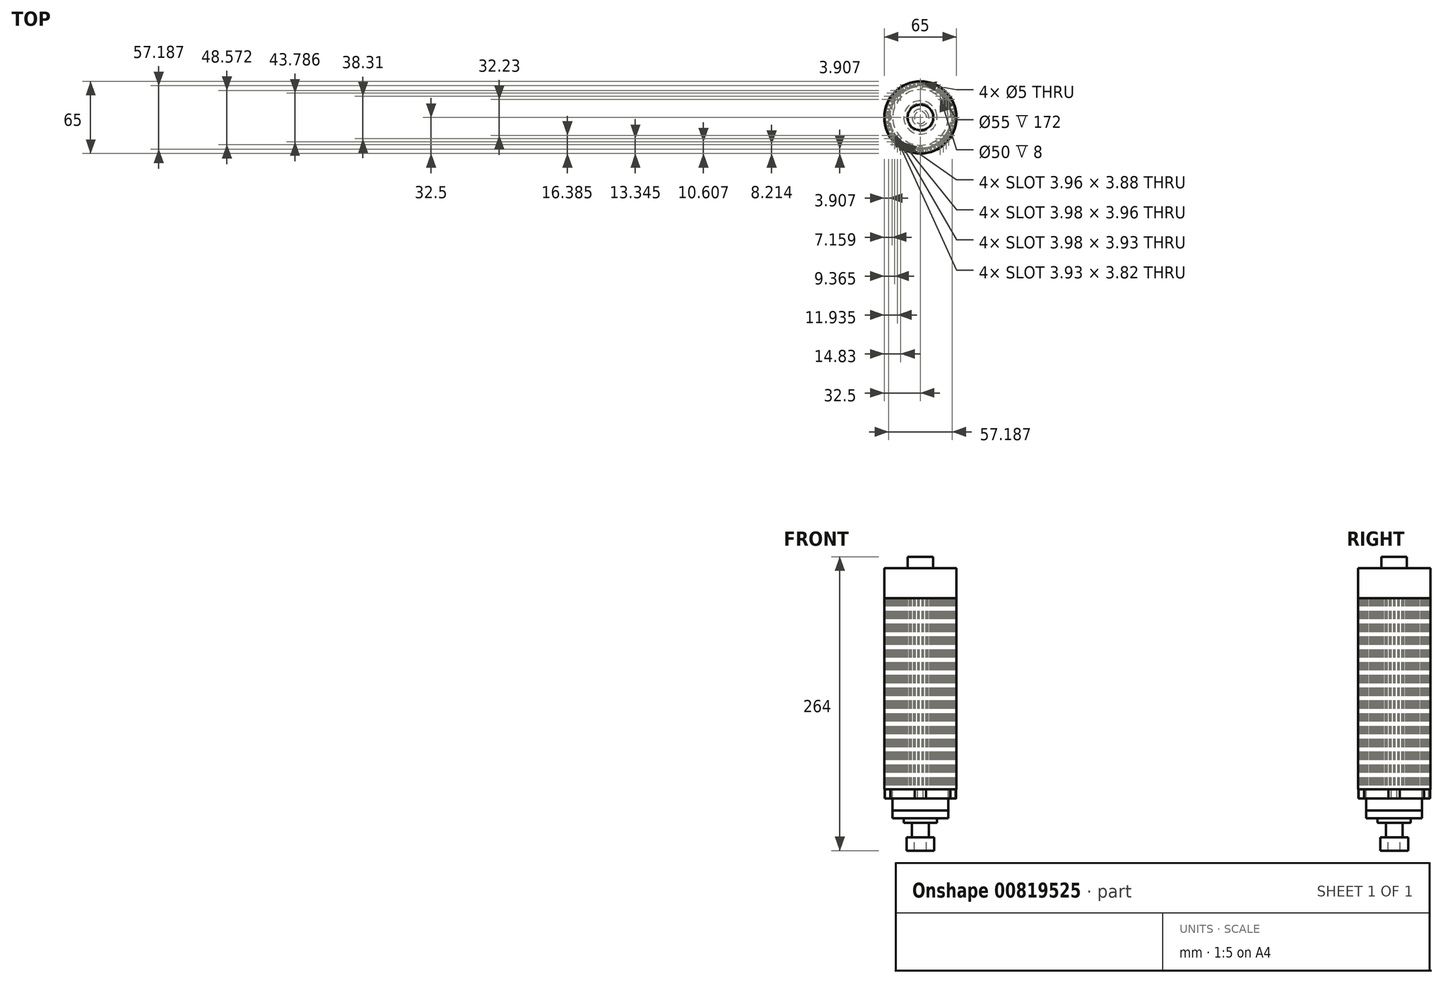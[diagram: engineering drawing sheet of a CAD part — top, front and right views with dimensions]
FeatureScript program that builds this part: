
annotation { "Feature Type Name" : "Feature", "Feature Type Description" : "" }
export const myFeature = defineFeature(function(context is Context, id is Id, definition is map)
    precondition{}
    {
        {
            var Q0;
            Q0=qCreatedBy(makeId("Top.planeOp"),FACE);
            var sketch = newSketch(context, id + "F0", { "sketchPlane" : qUnion([Q0])});
            skCircle(sketch, "E0", {"center": v(0, 0) * mm, "radius": 27.5 * mm});
            skCircle(sketch, "E1", {"center": v(0, 0) * mm, "radius": 32.5 * mm});
            skArc(sketch, "E2", {"start": v(1.37, 31.47) * mm, "mid": v(0, 31.5) * mm, "end": v(-1.37, 31.47) * mm});
            skArc(sketch, "E3", {"start": v(1.24, 28.47) * mm, "mid": v(0, 28.5) * mm, "end": v(-1.24, 28.47) * mm});
            skLineSegment(sketch, "E4", {"start": v(-1.37, 31.47) * mm, "end": v(-1.24, 28.47) * mm});
            skLineSegment(sketch, "E5", {"start": v(-1.24, 28.47) * mm, "end": v(0, 0) * mm, "construction": true});
            skLineSegment(sketch, "E6", {"start": v(0, 0) * mm, "end": v(1.24, 28.47) * mm, "construction": true});
            skLineSegment(sketch, "E7", {"start": v(1.24, 28.47) * mm, "end": v(1.37, 31.47) * mm});
            skArc(sketch, "E8.1.0", {"start": v(-2.58, 31.4) * mm, "mid": v(-3.95, 31.25) * mm, "end": v(-5.3, 31.05) * mm});
            skLineSegment(sketch, "E8.1.1", {"start": v(-5.3, 31.05) * mm, "end": v(-4.8, 28.1) * mm});
            skArc(sketch, "E8.1.2", {"start": v(-2.34, 28.4) * mm, "mid": v(-3.57, 28.28) * mm, "end": v(-4.8, 28.1) * mm});
            skLineSegment(sketch, "E8.1.3", {"start": v(-2.34, 28.4) * mm, "end": v(-2.58, 31.4) * mm});
            skArc(sketch, "E8.2.0", {"start": v(-6.5, 30.82) * mm, "mid": v(-7.83, 30.51) * mm, "end": v(-9.16, 30.14) * mm});
            skLineSegment(sketch, "E8.2.1", {"start": v(-9.16, 30.14) * mm, "end": v(-8.29, 27.27) * mm});
            skArc(sketch, "E8.2.2", {"start": v(-5.88, 27.89) * mm, "mid": v(-7.09, 27.6) * mm, "end": v(-8.29, 27.27) * mm});
            skLineSegment(sketch, "E8.2.3", {"start": v(-5.88, 27.89) * mm, "end": v(-6.5, 30.82) * mm});
            skArc(sketch, "E8.3.0", {"start": v(-10.3, 29.77) * mm, "mid": v(-11.6, 29.29) * mm, "end": v(-12.86, 28.75) * mm});
            skLineSegment(sketch, "E8.3.1", {"start": v(-12.86, 28.75) * mm, "end": v(-11.64, 26.02) * mm});
            skArc(sketch, "E8.3.2", {"start": v(-9.33, 26.93) * mm, "mid": v(-10.5, 26.5) * mm, "end": v(-11.64, 26.02) * mm});
            skLineSegment(sketch, "E8.3.3", {"start": v(-9.33, 26.93) * mm, "end": v(-10.3, 29.77) * mm});
            skArc(sketch, "E8.4.0", {"start": v(-13.96, 28.24) * mm, "mid": v(-15.18, 27.6) * mm, "end": v(-16.36, 26.92) * mm});
            skLineSegment(sketch, "E8.4.1", {"start": v(-16.36, 26.92) * mm, "end": v(-14.8, 24.35) * mm});
            skArc(sketch, "E8.4.2", {"start": v(-12.63, 25.55) * mm, "mid": v(-13.73, 24.97) * mm, "end": v(-14.8, 24.35) * mm});
            skLineSegment(sketch, "E8.4.3", {"start": v(-12.63, 25.55) * mm, "end": v(-13.96, 28.24) * mm});
            skArc(sketch, "E8.5.0", {"start": v(-17.39, 26.27) * mm, "mid": v(-18.52, 25.48) * mm, "end": v(-19.6, 24.65) * mm});
            skLineSegment(sketch, "E8.5.1", {"start": v(-19.6, 24.65) * mm, "end": v(-17.74, 22.3) * mm});
            skArc(sketch, "E8.5.2", {"start": v(-15.73, 23.77) * mm, "mid": v(-16.75, 23.06) * mm, "end": v(-17.74, 22.3) * mm});
            skLineSegment(sketch, "E8.5.3", {"start": v(-15.73, 23.77) * mm, "end": v(-17.39, 26.27) * mm});
            skArc(sketch, "E8.6.0", {"start": v(-20.54, 23.88) * mm, "mid": v(-21.56, 22.96) * mm, "end": v(-22.54, 22) * mm});
            skLineSegment(sketch, "E8.6.1", {"start": v(-22.54, 22) * mm, "end": v(-20.4, 19.9) * mm});
            skArc(sketch, "E8.6.2", {"start": v(-18.58, 21.6) * mm, "mid": v(-19.5, 20.78) * mm, "end": v(-20.4, 19.9) * mm});
            skLineSegment(sketch, "E8.6.3", {"start": v(-18.58, 21.6) * mm, "end": v(-20.54, 23.88) * mm});
            skArc(sketch, "E8.7.0", {"start": v(-23.37, 21.12) * mm, "mid": v(-24.27, 20.08) * mm, "end": v(-25.12, 19) * mm});
            skLineSegment(sketch, "E8.7.1", {"start": v(-25.12, 19) * mm, "end": v(-22.73, 17.2) * mm});
            skArc(sketch, "E8.7.2", {"start": v(-21.15, 19.1) * mm, "mid": v(-21.96, 18.17) * mm, "end": v(-22.73, 17.2) * mm});
            skLineSegment(sketch, "E8.7.3", {"start": v(-21.15, 19.1) * mm, "end": v(-23.37, 21.12) * mm});
            skArc(sketch, "E8.8.0", {"start": v(-25.83, 18.02) * mm, "mid": v(-26.6, 16.88) * mm, "end": v(-27.3, 15.7) * mm});
            skLineSegment(sketch, "E8.8.1", {"start": v(-27.3, 15.7) * mm, "end": v(-24.7, 14.2) * mm});
            skArc(sketch, "E8.8.2", {"start": v(-23.37, 16.3) * mm, "mid": v(-24.06, 15.27) * mm, "end": v(-24.7, 14.2) * mm});
            skLineSegment(sketch, "E8.8.3", {"start": v(-23.37, 16.3) * mm, "end": v(-25.83, 18.02) * mm});
            skArc(sketch, "E8.9.0", {"start": v(-27.89, 14.64) * mm, "mid": v(-28.5, 13.41) * mm, "end": v(-29.06, 12.16) * mm});
            skLineSegment(sketch, "E8.9.1", {"start": v(-29.06, 12.16) * mm, "end": v(-26.3, 11) * mm});
            skArc(sketch, "E8.9.2", {"start": v(-25.23, 13.25) * mm, "mid": v(-25.79, 12.13) * mm, "end": v(-26.3, 11) * mm});
            skLineSegment(sketch, "E8.9.3", {"start": v(-25.23, 13.25) * mm, "end": v(-27.89, 14.64) * mm});
            skArc(sketch, "E8.10.0", {"start": v(-29.5, 11.03) * mm, "mid": v(-29.96, 9.73) * mm, "end": v(-30.35, 8.42) * mm});
            skLineSegment(sketch, "E8.10.1", {"start": v(-30.35, 8.42) * mm, "end": v(-27.46, 7.62) * mm});
            skArc(sketch, "E8.10.2", {"start": v(-26.7, 9.98) * mm, "mid": v(-27.1, 8.8) * mm, "end": v(-27.46, 7.62) * mm});
            skLineSegment(sketch, "E8.10.3", {"start": v(-26.7, 9.98) * mm, "end": v(-29.5, 11.03) * mm});
            skArc(sketch, "E8.11.0", {"start": v(-30.66, 7.25) * mm, "mid": v(-30.94, 5.9) * mm, "end": v(-31.17, 4.55) * mm});
            skLineSegment(sketch, "E8.11.1", {"start": v(-31.17, 4.55) * mm, "end": v(-28.2, 4.11) * mm});
            skArc(sketch, "E8.11.2", {"start": v(-27.74, 6.56) * mm, "mid": v(-28, 5.34) * mm, "end": v(-28.2, 4.11) * mm});
            skLineSegment(sketch, "E8.11.3", {"start": v(-27.74, 6.56) * mm, "end": v(-30.66, 7.25) * mm});
            skArc(sketch, "E8.12.0", {"start": v(-31.32, 3.35) * mm, "mid": v(-31.44, 1.98) * mm, "end": v(-31.5, 0.6) * mm});
            skLineSegment(sketch, "E8.12.1", {"start": v(-31.5, 0.6) * mm, "end": v(-28.5, 0.55) * mm});
            skArc(sketch, "E8.12.2", {"start": v(-28.34, 3.03) * mm, "mid": v(-28.44, 1.79) * mm, "end": v(-28.5, 0.55) * mm});
            skLineSegment(sketch, "E8.12.3", {"start": v(-28.34, 3.03) * mm, "end": v(-31.32, 3.35) * mm});
            skArc(sketch, "E8.13.0", {"start": v(-31.5, -0.6) * mm, "mid": v(-31.44, -1.98) * mm, "end": v(-31.32, -3.35) * mm});
            skLineSegment(sketch, "E8.13.1", {"start": v(-31.32, -3.35) * mm, "end": v(-28.34, -3.03) * mm});
            skArc(sketch, "E8.13.2", {"start": v(-28.5, -0.55) * mm, "mid": v(-28.44, -1.79) * mm, "end": v(-28.34, -3.03) * mm});
            skLineSegment(sketch, "E8.13.3", {"start": v(-28.5, -0.55) * mm, "end": v(-31.5, -0.6) * mm});
            skArc(sketch, "E8.14.0", {"start": v(-31.17, -4.55) * mm, "mid": v(-30.94, -5.9) * mm, "end": v(-30.66, -7.25) * mm});
            skLineSegment(sketch, "E8.14.1", {"start": v(-30.66, -7.25) * mm, "end": v(-27.74, -6.56) * mm});
            skArc(sketch, "E8.14.2", {"start": v(-28.2, -4.11) * mm, "mid": v(-28, -5.34) * mm, "end": v(-27.74, -6.56) * mm});
            skLineSegment(sketch, "E8.14.3", {"start": v(-28.2, -4.11) * mm, "end": v(-31.17, -4.55) * mm});
            skArc(sketch, "E8.15.0", {"start": v(-30.35, -8.42) * mm, "mid": v(-29.96, -9.73) * mm, "end": v(-29.5, -11.03) * mm});
            skLineSegment(sketch, "E8.15.1", {"start": v(-29.5, -11.03) * mm, "end": v(-26.7, -9.98) * mm});
            skArc(sketch, "E8.15.2", {"start": v(-27.46, -7.62) * mm, "mid": v(-27.1, -8.8) * mm, "end": v(-26.7, -9.98) * mm});
            skLineSegment(sketch, "E8.15.3", {"start": v(-27.46, -7.62) * mm, "end": v(-30.35, -8.42) * mm});
            skArc(sketch, "E8.16.0", {"start": v(-29.06, -12.16) * mm, "mid": v(-28.5, -13.41) * mm, "end": v(-27.89, -14.64) * mm});
            skLineSegment(sketch, "E8.16.1", {"start": v(-27.89, -14.64) * mm, "end": v(-25.23, -13.25) * mm});
            skArc(sketch, "E8.16.2", {"start": v(-26.3, -11) * mm, "mid": v(-25.79, -12.13) * mm, "end": v(-25.23, -13.25) * mm});
            skLineSegment(sketch, "E8.16.3", {"start": v(-26.3, -11) * mm, "end": v(-29.06, -12.16) * mm});
            skArc(sketch, "E8.17.0", {"start": v(-27.3, -15.7) * mm, "mid": v(-26.6, -16.88) * mm, "end": v(-25.83, -18.02) * mm});
            skLineSegment(sketch, "E8.17.1", {"start": v(-25.83, -18.02) * mm, "end": v(-23.37, -16.3) * mm});
            skArc(sketch, "E8.17.2", {"start": v(-24.7, -14.2) * mm, "mid": v(-24.06, -15.27) * mm, "end": v(-23.37, -16.3) * mm});
            skLineSegment(sketch, "E8.17.3", {"start": v(-24.7, -14.2) * mm, "end": v(-27.3, -15.7) * mm});
            skArc(sketch, "E8.18.0", {"start": v(-25.12, -19) * mm, "mid": v(-24.27, -20.08) * mm, "end": v(-23.37, -21.12) * mm});
            skLineSegment(sketch, "E8.18.1", {"start": v(-23.37, -21.12) * mm, "end": v(-21.15, -19.1) * mm});
            skArc(sketch, "E8.18.2", {"start": v(-22.73, -17.2) * mm, "mid": v(-21.96, -18.17) * mm, "end": v(-21.15, -19.1) * mm});
            skLineSegment(sketch, "E8.18.3", {"start": v(-22.73, -17.2) * mm, "end": v(-25.12, -19) * mm});
            skArc(sketch, "E8.19.0", {"start": v(-22.54, -22) * mm, "mid": v(-21.56, -22.96) * mm, "end": v(-20.54, -23.88) * mm});
            skLineSegment(sketch, "E8.19.1", {"start": v(-20.54, -23.88) * mm, "end": v(-18.58, -21.6) * mm});
            skArc(sketch, "E8.19.2", {"start": v(-20.4, -19.9) * mm, "mid": v(-19.5, -20.78) * mm, "end": v(-18.58, -21.6) * mm});
            skLineSegment(sketch, "E8.19.3", {"start": v(-20.4, -19.9) * mm, "end": v(-22.54, -22) * mm});
            skArc(sketch, "E8.20.0", {"start": v(-19.6, -24.65) * mm, "mid": v(-18.52, -25.48) * mm, "end": v(-17.39, -26.27) * mm});
            skLineSegment(sketch, "E8.20.1", {"start": v(-17.39, -26.27) * mm, "end": v(-15.73, -23.77) * mm});
            skArc(sketch, "E8.20.2", {"start": v(-17.74, -22.3) * mm, "mid": v(-16.75, -23.06) * mm, "end": v(-15.73, -23.77) * mm});
            skLineSegment(sketch, "E8.20.3", {"start": v(-17.74, -22.3) * mm, "end": v(-19.6, -24.65) * mm});
            skArc(sketch, "E8.21.0", {"start": v(-16.36, -26.92) * mm, "mid": v(-15.18, -27.6) * mm, "end": v(-13.96, -28.24) * mm});
            skLineSegment(sketch, "E8.21.1", {"start": v(-13.96, -28.24) * mm, "end": v(-12.63, -25.55) * mm});
            skArc(sketch, "E8.21.2", {"start": v(-14.8, -24.35) * mm, "mid": v(-13.73, -24.97) * mm, "end": v(-12.63, -25.55) * mm});
            skLineSegment(sketch, "E8.21.3", {"start": v(-14.8, -24.35) * mm, "end": v(-16.36, -26.92) * mm});
            skArc(sketch, "E8.22.0", {"start": v(-12.86, -28.75) * mm, "mid": v(-11.6, -29.29) * mm, "end": v(-10.3, -29.77) * mm});
            skLineSegment(sketch, "E8.22.1", {"start": v(-10.3, -29.77) * mm, "end": v(-9.33, -26.93) * mm});
            skArc(sketch, "E8.22.2", {"start": v(-11.64, -26.02) * mm, "mid": v(-10.5, -26.5) * mm, "end": v(-9.33, -26.93) * mm});
            skLineSegment(sketch, "E8.22.3", {"start": v(-11.64, -26.02) * mm, "end": v(-12.86, -28.75) * mm});
            skArc(sketch, "E8.23.0", {"start": v(-9.16, -30.14) * mm, "mid": v(-7.83, -30.51) * mm, "end": v(-6.5, -30.82) * mm});
            skLineSegment(sketch, "E8.23.1", {"start": v(-6.5, -30.82) * mm, "end": v(-5.88, -27.89) * mm});
            skArc(sketch, "E8.23.2", {"start": v(-8.29, -27.27) * mm, "mid": v(-7.09, -27.6) * mm, "end": v(-5.88, -27.89) * mm});
            skLineSegment(sketch, "E8.23.3", {"start": v(-8.29, -27.27) * mm, "end": v(-9.16, -30.14) * mm});
            skArc(sketch, "E8.24.0", {"start": v(-5.3, -31.05) * mm, "mid": v(-3.95, -31.25) * mm, "end": v(-2.58, -31.4) * mm});
            skLineSegment(sketch, "E8.24.1", {"start": v(-2.58, -31.4) * mm, "end": v(-2.34, -28.4) * mm});
            skArc(sketch, "E8.24.2", {"start": v(-4.8, -28.1) * mm, "mid": v(-3.57, -28.28) * mm, "end": v(-2.34, -28.4) * mm});
            skLineSegment(sketch, "E8.24.3", {"start": v(-4.8, -28.1) * mm, "end": v(-5.3, -31.05) * mm});
            skArc(sketch, "E8.25.0", {"start": v(-1.37, -31.47) * mm, "mid": v(0, -31.5) * mm, "end": v(1.37, -31.47) * mm});
            skLineSegment(sketch, "E8.25.1", {"start": v(1.37, -31.47) * mm, "end": v(1.24, -28.47) * mm});
            skArc(sketch, "E8.25.2", {"start": v(-1.24, -28.47) * mm, "mid": v(0, -28.5) * mm, "end": v(1.24, -28.47) * mm});
            skLineSegment(sketch, "E8.25.3", {"start": v(-1.24, -28.47) * mm, "end": v(-1.37, -31.47) * mm});
            skArc(sketch, "E8.26.0", {"start": v(2.58, -31.4) * mm, "mid": v(3.95, -31.25) * mm, "end": v(5.3, -31.05) * mm});
            skLineSegment(sketch, "E8.26.1", {"start": v(5.3, -31.05) * mm, "end": v(4.8, -28.1) * mm});
            skArc(sketch, "E8.26.2", {"start": v(2.34, -28.4) * mm, "mid": v(3.57, -28.28) * mm, "end": v(4.8, -28.1) * mm});
            skLineSegment(sketch, "E8.26.3", {"start": v(2.34, -28.4) * mm, "end": v(2.58, -31.4) * mm});
            skArc(sketch, "E8.27.0", {"start": v(6.5, -30.82) * mm, "mid": v(7.83, -30.51) * mm, "end": v(9.16, -30.14) * mm});
            skLineSegment(sketch, "E8.27.1", {"start": v(9.16, -30.14) * mm, "end": v(8.29, -27.27) * mm});
            skArc(sketch, "E8.27.2", {"start": v(5.88, -27.89) * mm, "mid": v(7.09, -27.6) * mm, "end": v(8.29, -27.27) * mm});
            skLineSegment(sketch, "E8.27.3", {"start": v(5.88, -27.89) * mm, "end": v(6.5, -30.82) * mm});
            skArc(sketch, "E8.28.0", {"start": v(10.3, -29.77) * mm, "mid": v(11.6, -29.29) * mm, "end": v(12.86, -28.75) * mm});
            skLineSegment(sketch, "E8.28.1", {"start": v(12.86, -28.75) * mm, "end": v(11.64, -26.02) * mm});
            skArc(sketch, "E8.28.2", {"start": v(9.33, -26.93) * mm, "mid": v(10.5, -26.5) * mm, "end": v(11.64, -26.02) * mm});
            skLineSegment(sketch, "E8.28.3", {"start": v(9.33, -26.93) * mm, "end": v(10.3, -29.77) * mm});
            skArc(sketch, "E8.29.0", {"start": v(13.96, -28.24) * mm, "mid": v(15.18, -27.6) * mm, "end": v(16.36, -26.92) * mm});
            skLineSegment(sketch, "E8.29.1", {"start": v(16.36, -26.92) * mm, "end": v(14.8, -24.35) * mm});
            skArc(sketch, "E8.29.2", {"start": v(12.63, -25.55) * mm, "mid": v(13.73, -24.97) * mm, "end": v(14.8, -24.35) * mm});
            skLineSegment(sketch, "E8.29.3", {"start": v(12.63, -25.55) * mm, "end": v(13.96, -28.24) * mm});
            skArc(sketch, "E8.30.0", {"start": v(17.39, -26.27) * mm, "mid": v(18.52, -25.48) * mm, "end": v(19.6, -24.65) * mm});
            skLineSegment(sketch, "E8.30.1", {"start": v(19.6, -24.65) * mm, "end": v(17.74, -22.3) * mm});
            skArc(sketch, "E8.30.2", {"start": v(15.73, -23.77) * mm, "mid": v(16.75, -23.06) * mm, "end": v(17.74, -22.3) * mm});
            skLineSegment(sketch, "E8.30.3", {"start": v(15.73, -23.77) * mm, "end": v(17.39, -26.27) * mm});
            skArc(sketch, "E8.31.0", {"start": v(20.54, -23.88) * mm, "mid": v(21.56, -22.96) * mm, "end": v(22.54, -22) * mm});
            skLineSegment(sketch, "E8.31.1", {"start": v(22.54, -22) * mm, "end": v(20.4, -19.9) * mm});
            skArc(sketch, "E8.31.2", {"start": v(18.58, -21.6) * mm, "mid": v(19.5, -20.78) * mm, "end": v(20.4, -19.9) * mm});
            skLineSegment(sketch, "E8.31.3", {"start": v(18.58, -21.6) * mm, "end": v(20.54, -23.88) * mm});
            skArc(sketch, "E8.32.0", {"start": v(23.37, -21.12) * mm, "mid": v(24.27, -20.08) * mm, "end": v(25.12, -19) * mm});
            skLineSegment(sketch, "E8.32.1", {"start": v(25.12, -19) * mm, "end": v(22.73, -17.2) * mm});
            skArc(sketch, "E8.32.2", {"start": v(21.15, -19.1) * mm, "mid": v(21.96, -18.17) * mm, "end": v(22.73, -17.2) * mm});
            skLineSegment(sketch, "E8.32.3", {"start": v(21.15, -19.1) * mm, "end": v(23.37, -21.12) * mm});
            skArc(sketch, "E8.33.0", {"start": v(25.83, -18.02) * mm, "mid": v(26.6, -16.88) * mm, "end": v(27.3, -15.7) * mm});
            skLineSegment(sketch, "E8.33.1", {"start": v(27.3, -15.7) * mm, "end": v(24.7, -14.2) * mm});
            skArc(sketch, "E8.33.2", {"start": v(23.37, -16.3) * mm, "mid": v(24.06, -15.27) * mm, "end": v(24.7, -14.2) * mm});
            skLineSegment(sketch, "E8.33.3", {"start": v(23.37, -16.3) * mm, "end": v(25.83, -18.02) * mm});
            skArc(sketch, "E8.34.0", {"start": v(27.89, -14.64) * mm, "mid": v(28.5, -13.41) * mm, "end": v(29.06, -12.16) * mm});
            skLineSegment(sketch, "E8.34.1", {"start": v(29.06, -12.16) * mm, "end": v(26.3, -11) * mm});
            skArc(sketch, "E8.34.2", {"start": v(25.23, -13.25) * mm, "mid": v(25.79, -12.13) * mm, "end": v(26.3, -11) * mm});
            skLineSegment(sketch, "E8.34.3", {"start": v(25.23, -13.25) * mm, "end": v(27.89, -14.64) * mm});
            skArc(sketch, "E8.35.0", {"start": v(29.5, -11.03) * mm, "mid": v(29.96, -9.73) * mm, "end": v(30.35, -8.42) * mm});
            skLineSegment(sketch, "E8.35.1", {"start": v(30.35, -8.42) * mm, "end": v(27.46, -7.62) * mm});
            skArc(sketch, "E8.35.2", {"start": v(26.7, -9.98) * mm, "mid": v(27.1, -8.8) * mm, "end": v(27.46, -7.62) * mm});
            skLineSegment(sketch, "E8.35.3", {"start": v(26.7, -9.98) * mm, "end": v(29.5, -11.03) * mm});
            skArc(sketch, "E8.36.0", {"start": v(30.66, -7.25) * mm, "mid": v(30.94, -5.9) * mm, "end": v(31.17, -4.55) * mm});
            skLineSegment(sketch, "E8.36.1", {"start": v(31.17, -4.55) * mm, "end": v(28.2, -4.11) * mm});
            skArc(sketch, "E8.36.2", {"start": v(27.74, -6.56) * mm, "mid": v(28, -5.34) * mm, "end": v(28.2, -4.11) * mm});
            skLineSegment(sketch, "E8.36.3", {"start": v(27.74, -6.56) * mm, "end": v(30.66, -7.25) * mm});
            skArc(sketch, "E8.37.0", {"start": v(31.32, -3.35) * mm, "mid": v(31.44, -1.98) * mm, "end": v(31.5, -0.6) * mm});
            skLineSegment(sketch, "E8.37.1", {"start": v(31.5, -0.6) * mm, "end": v(28.5, -0.55) * mm});
            skArc(sketch, "E8.37.2", {"start": v(28.34, -3.03) * mm, "mid": v(28.44, -1.79) * mm, "end": v(28.5, -0.55) * mm});
            skLineSegment(sketch, "E8.37.3", {"start": v(28.34, -3.03) * mm, "end": v(31.32, -3.35) * mm});
            skArc(sketch, "E8.38.0", {"start": v(31.5, 0.6) * mm, "mid": v(31.44, 1.98) * mm, "end": v(31.32, 3.35) * mm});
            skLineSegment(sketch, "E8.38.1", {"start": v(31.32, 3.35) * mm, "end": v(28.34, 3.03) * mm});
            skArc(sketch, "E8.38.2", {"start": v(28.5, 0.55) * mm, "mid": v(28.44, 1.79) * mm, "end": v(28.34, 3.03) * mm});
            skLineSegment(sketch, "E8.38.3", {"start": v(28.5, 0.55) * mm, "end": v(31.5, 0.6) * mm});
            skArc(sketch, "E8.39.0", {"start": v(31.17, 4.55) * mm, "mid": v(30.94, 5.9) * mm, "end": v(30.66, 7.25) * mm});
            skLineSegment(sketch, "E8.39.1", {"start": v(30.66, 7.25) * mm, "end": v(27.74, 6.56) * mm});
            skArc(sketch, "E8.39.2", {"start": v(28.2, 4.11) * mm, "mid": v(28, 5.34) * mm, "end": v(27.74, 6.56) * mm});
            skLineSegment(sketch, "E8.39.3", {"start": v(28.2, 4.11) * mm, "end": v(31.17, 4.55) * mm});
            skArc(sketch, "E8.40.0", {"start": v(30.35, 8.42) * mm, "mid": v(29.96, 9.73) * mm, "end": v(29.5, 11.03) * mm});
            skLineSegment(sketch, "E8.40.1", {"start": v(29.5, 11.03) * mm, "end": v(26.7, 9.98) * mm});
            skArc(sketch, "E8.40.2", {"start": v(27.46, 7.62) * mm, "mid": v(27.1, 8.8) * mm, "end": v(26.7, 9.98) * mm});
            skLineSegment(sketch, "E8.40.3", {"start": v(27.46, 7.62) * mm, "end": v(30.35, 8.42) * mm});
            skArc(sketch, "E8.41.0", {"start": v(29.06, 12.16) * mm, "mid": v(28.5, 13.41) * mm, "end": v(27.89, 14.64) * mm});
            skLineSegment(sketch, "E8.41.1", {"start": v(27.89, 14.64) * mm, "end": v(25.23, 13.25) * mm});
            skArc(sketch, "E8.41.2", {"start": v(26.3, 11) * mm, "mid": v(25.79, 12.13) * mm, "end": v(25.23, 13.25) * mm});
            skLineSegment(sketch, "E8.41.3", {"start": v(26.3, 11) * mm, "end": v(29.06, 12.16) * mm});
            skArc(sketch, "E8.42.0", {"start": v(27.3, 15.7) * mm, "mid": v(26.6, 16.88) * mm, "end": v(25.83, 18.02) * mm});
            skLineSegment(sketch, "E8.42.1", {"start": v(25.83, 18.02) * mm, "end": v(23.37, 16.3) * mm});
            skArc(sketch, "E8.42.2", {"start": v(24.7, 14.2) * mm, "mid": v(24.06, 15.27) * mm, "end": v(23.37, 16.3) * mm});
            skLineSegment(sketch, "E8.42.3", {"start": v(24.7, 14.2) * mm, "end": v(27.3, 15.7) * mm});
            skArc(sketch, "E8.43.0", {"start": v(25.12, 19) * mm, "mid": v(24.27, 20.08) * mm, "end": v(23.37, 21.12) * mm});
            skLineSegment(sketch, "E8.43.1", {"start": v(23.37, 21.12) * mm, "end": v(21.15, 19.1) * mm});
            skArc(sketch, "E8.43.2", {"start": v(22.73, 17.2) * mm, "mid": v(21.96, 18.17) * mm, "end": v(21.15, 19.1) * mm});
            skLineSegment(sketch, "E8.43.3", {"start": v(22.73, 17.2) * mm, "end": v(25.12, 19) * mm});
            skArc(sketch, "E8.44.0", {"start": v(22.54, 22) * mm, "mid": v(21.56, 22.96) * mm, "end": v(20.54, 23.88) * mm});
            skLineSegment(sketch, "E8.44.1", {"start": v(20.54, 23.88) * mm, "end": v(18.58, 21.6) * mm});
            skArc(sketch, "E8.44.2", {"start": v(20.4, 19.9) * mm, "mid": v(19.5, 20.78) * mm, "end": v(18.58, 21.6) * mm});
            skLineSegment(sketch, "E8.44.3", {"start": v(20.4, 19.9) * mm, "end": v(22.54, 22) * mm});
            skArc(sketch, "E8.45.0", {"start": v(19.6, 24.65) * mm, "mid": v(18.52, 25.48) * mm, "end": v(17.39, 26.27) * mm});
            skLineSegment(sketch, "E8.45.1", {"start": v(17.39, 26.27) * mm, "end": v(15.73, 23.77) * mm});
            skArc(sketch, "E8.45.2", {"start": v(17.74, 22.3) * mm, "mid": v(16.75, 23.06) * mm, "end": v(15.73, 23.77) * mm});
            skLineSegment(sketch, "E8.45.3", {"start": v(17.74, 22.3) * mm, "end": v(19.6, 24.65) * mm});
            skArc(sketch, "E8.46.0", {"start": v(16.36, 26.92) * mm, "mid": v(15.18, 27.6) * mm, "end": v(13.96, 28.24) * mm});
            skLineSegment(sketch, "E8.46.1", {"start": v(13.96, 28.24) * mm, "end": v(12.63, 25.55) * mm});
            skArc(sketch, "E8.46.2", {"start": v(14.8, 24.35) * mm, "mid": v(13.73, 24.97) * mm, "end": v(12.63, 25.55) * mm});
            skLineSegment(sketch, "E8.46.3", {"start": v(14.8, 24.35) * mm, "end": v(16.36, 26.92) * mm});
            skArc(sketch, "E8.47.0", {"start": v(12.86, 28.75) * mm, "mid": v(11.6, 29.29) * mm, "end": v(10.3, 29.77) * mm});
            skLineSegment(sketch, "E8.47.1", {"start": v(10.3, 29.77) * mm, "end": v(9.33, 26.93) * mm});
            skArc(sketch, "E8.47.2", {"start": v(11.64, 26.02) * mm, "mid": v(10.5, 26.5) * mm, "end": v(9.33, 26.93) * mm});
            skLineSegment(sketch, "E8.47.3", {"start": v(11.64, 26.02) * mm, "end": v(12.86, 28.75) * mm});
            skArc(sketch, "E8.48.0", {"start": v(9.16, 30.14) * mm, "mid": v(7.83, 30.51) * mm, "end": v(6.5, 30.82) * mm});
            skLineSegment(sketch, "E8.48.1", {"start": v(6.5, 30.82) * mm, "end": v(5.88, 27.89) * mm});
            skArc(sketch, "E8.48.2", {"start": v(8.29, 27.27) * mm, "mid": v(7.09, 27.6) * mm, "end": v(5.88, 27.89) * mm});
            skLineSegment(sketch, "E8.48.3", {"start": v(8.29, 27.27) * mm, "end": v(9.16, 30.14) * mm});
            skArc(sketch, "E8.49.0", {"start": v(5.3, 31.05) * mm, "mid": v(3.95, 31.25) * mm, "end": v(2.58, 31.4) * mm});
            skLineSegment(sketch, "E8.49.1", {"start": v(2.58, 31.4) * mm, "end": v(2.34, 28.4) * mm});
            skArc(sketch, "E8.49.2", {"start": v(4.8, 28.1) * mm, "mid": v(3.57, 28.28) * mm, "end": v(2.34, 28.4) * mm});
            skLineSegment(sketch, "E8.49.3", {"start": v(4.8, 28.1) * mm, "end": v(5.3, 31.05) * mm});
            skSolve(sketch);
        }
        {
            var Q0;
            Q0=makeQuery(id+"F0.imprint","IMPRINT",FACE,{"disambiguationData":[TD([[makeQuery(id+"F0.imprint","IMPRINT",EDGE,{"derivedFrom":sQuery(id+"F0.wireOp",EDGE,"E0")}),-1.0]])]});
            extrude(context, id + "F1", {"entities" : qUnion([Q0]), "depth" : 172 * mm, "offsetDistance" : 25.4 * mm});
        }
        {
            var Q0;
            Q0=makeQuery(id+"F1.opExtrude","CAP_FACE",FACE,{"disambiguationData":[OSD([sQuery(id+"F0.wireOp",EDGE,"E0"),sQuery(id+"F0.wireOp",EDGE,"E1"),sQuery(id+"F0.wireOp",EDGE,"E2"),sQuery(id+"F0.wireOp",EDGE,"E3"),sQuery(id+"F0.wireOp",EDGE,"E4"),sQuery(id+"F0.wireOp",EDGE,"E7"),sQuery(id+"F0.wireOp",EDGE,"E8.1.0"),sQuery(id+"F0.wireOp",EDGE,"E8.1.1"),sQuery(id+"F0.wireOp",EDGE,"E8.1.2"),sQuery(id+"F0.wireOp",EDGE,"E8.1.3"),sQuery(id+"F0.wireOp",EDGE,"E8.2.0"),sQuery(id+"F0.wireOp",EDGE,"E8.2.1"),sQuery(id+"F0.wireOp",EDGE,"E8.2.2"),sQuery(id+"F0.wireOp",EDGE,"E8.2.3"),sQuery(id+"F0.wireOp",EDGE,"E8.3.0"),sQuery(id+"F0.wireOp",EDGE,"E8.3.1"),sQuery(id+"F0.wireOp",EDGE,"E8.3.2"),sQuery(id+"F0.wireOp",EDGE,"E8.3.3"),sQuery(id+"F0.wireOp",EDGE,"E8.4.0"),sQuery(id+"F0.wireOp",EDGE,"E8.4.1"),sQuery(id+"F0.wireOp",EDGE,"E8.4.2"),sQuery(id+"F0.wireOp",EDGE,"E8.4.3"),sQuery(id+"F0.wireOp",EDGE,"E8.5.0"),sQuery(id+"F0.wireOp",EDGE,"E8.5.1"),sQuery(id+"F0.wireOp",EDGE,"E8.5.2"),sQuery(id+"F0.wireOp",EDGE,"E8.5.3"),sQuery(id+"F0.wireOp",EDGE,"E8.6.0"),sQuery(id+"F0.wireOp",EDGE,"E8.6.1"),sQuery(id+"F0.wireOp",EDGE,"E8.6.2"),sQuery(id+"F0.wireOp",EDGE,"E8.6.3"),sQuery(id+"F0.wireOp",EDGE,"E8.7.0"),sQuery(id+"F0.wireOp",EDGE,"E8.7.1"),sQuery(id+"F0.wireOp",EDGE,"E8.7.2"),sQuery(id+"F0.wireOp",EDGE,"E8.7.3"),sQuery(id+"F0.wireOp",EDGE,"E8.8.0"),sQuery(id+"F0.wireOp",EDGE,"E8.8.1"),sQuery(id+"F0.wireOp",EDGE,"E8.8.2"),sQuery(id+"F0.wireOp",EDGE,"E8.8.3"),sQuery(id+"F0.wireOp",EDGE,"E8.9.0"),sQuery(id+"F0.wireOp",EDGE,"E8.9.1"),sQuery(id+"F0.wireOp",EDGE,"E8.9.2"),sQuery(id+"F0.wireOp",EDGE,"E8.9.3"),sQuery(id+"F0.wireOp",EDGE,"E8.10.0"),sQuery(id+"F0.wireOp",EDGE,"E8.10.1"),sQuery(id+"F0.wireOp",EDGE,"E8.10.2"),sQuery(id+"F0.wireOp",EDGE,"E8.10.3"),sQuery(id+"F0.wireOp",EDGE,"E8.11.0"),sQuery(id+"F0.wireOp",EDGE,"E8.11.1"),sQuery(id+"F0.wireOp",EDGE,"E8.11.2"),sQuery(id+"F0.wireOp",EDGE,"E8.11.3"),sQuery(id+"F0.wireOp",EDGE,"E8.12.0"),sQuery(id+"F0.wireOp",EDGE,"E8.12.1"),sQuery(id+"F0.wireOp",EDGE,"E8.12.2"),sQuery(id+"F0.wireOp",EDGE,"E8.12.3"),sQuery(id+"F0.wireOp",EDGE,"E8.13.0"),sQuery(id+"F0.wireOp",EDGE,"E8.13.1"),sQuery(id+"F0.wireOp",EDGE,"E8.13.2"),sQuery(id+"F0.wireOp",EDGE,"E8.13.3"),sQuery(id+"F0.wireOp",EDGE,"E8.14.0"),sQuery(id+"F0.wireOp",EDGE,"E8.14.1"),sQuery(id+"F0.wireOp",EDGE,"E8.14.2"),sQuery(id+"F0.wireOp",EDGE,"E8.14.3"),sQuery(id+"F0.wireOp",EDGE,"E8.15.0"),sQuery(id+"F0.wireOp",EDGE,"E8.15.1"),sQuery(id+"F0.wireOp",EDGE,"E8.15.2"),sQuery(id+"F0.wireOp",EDGE,"E8.15.3"),sQuery(id+"F0.wireOp",EDGE,"E8.16.0"),sQuery(id+"F0.wireOp",EDGE,"E8.16.1"),sQuery(id+"F0.wireOp",EDGE,"E8.16.2"),sQuery(id+"F0.wireOp",EDGE,"E8.16.3"),sQuery(id+"F0.wireOp",EDGE,"E8.17.0"),sQuery(id+"F0.wireOp",EDGE,"E8.17.1"),sQuery(id+"F0.wireOp",EDGE,"E8.17.2"),sQuery(id+"F0.wireOp",EDGE,"E8.17.3"),sQuery(id+"F0.wireOp",EDGE,"E8.18.0"),sQuery(id+"F0.wireOp",EDGE,"E8.18.1"),sQuery(id+"F0.wireOp",EDGE,"E8.18.2"),sQuery(id+"F0.wireOp",EDGE,"E8.18.3"),sQuery(id+"F0.wireOp",EDGE,"E8.19.0"),sQuery(id+"F0.wireOp",EDGE,"E8.19.1"),sQuery(id+"F0.wireOp",EDGE,"E8.19.2"),sQuery(id+"F0.wireOp",EDGE,"E8.19.3"),sQuery(id+"F0.wireOp",EDGE,"E8.20.0"),sQuery(id+"F0.wireOp",EDGE,"E8.20.1"),sQuery(id+"F0.wireOp",EDGE,"E8.20.2"),sQuery(id+"F0.wireOp",EDGE,"E8.20.3"),sQuery(id+"F0.wireOp",EDGE,"E8.21.0"),sQuery(id+"F0.wireOp",EDGE,"E8.21.1"),sQuery(id+"F0.wireOp",EDGE,"E8.21.2"),sQuery(id+"F0.wireOp",EDGE,"E8.21.3"),sQuery(id+"F0.wireOp",EDGE,"E8.22.0"),sQuery(id+"F0.wireOp",EDGE,"E8.22.1"),sQuery(id+"F0.wireOp",EDGE,"E8.22.2"),sQuery(id+"F0.wireOp",EDGE,"E8.22.3"),sQuery(id+"F0.wireOp",EDGE,"E8.23.0"),sQuery(id+"F0.wireOp",EDGE,"E8.23.1"),sQuery(id+"F0.wireOp",EDGE,"E8.23.2"),sQuery(id+"F0.wireOp",EDGE,"E8.23.3"),sQuery(id+"F0.wireOp",EDGE,"E8.24.0"),sQuery(id+"F0.wireOp",EDGE,"E8.24.1"),sQuery(id+"F0.wireOp",EDGE,"E8.24.2"),sQuery(id+"F0.wireOp",EDGE,"E8.24.3"),sQuery(id+"F0.wireOp",EDGE,"E8.25.0"),sQuery(id+"F0.wireOp",EDGE,"E8.25.1"),sQuery(id+"F0.wireOp",EDGE,"E8.25.2"),sQuery(id+"F0.wireOp",EDGE,"E8.25.3"),sQuery(id+"F0.wireOp",EDGE,"E8.26.0"),sQuery(id+"F0.wireOp",EDGE,"E8.26.1"),sQuery(id+"F0.wireOp",EDGE,"E8.26.2"),sQuery(id+"F0.wireOp",EDGE,"E8.26.3"),sQuery(id+"F0.wireOp",EDGE,"E8.27.0"),sQuery(id+"F0.wireOp",EDGE,"E8.27.1"),sQuery(id+"F0.wireOp",EDGE,"E8.27.2"),sQuery(id+"F0.wireOp",EDGE,"E8.27.3"),sQuery(id+"F0.wireOp",EDGE,"E8.28.0"),sQuery(id+"F0.wireOp",EDGE,"E8.28.1"),sQuery(id+"F0.wireOp",EDGE,"E8.28.2"),sQuery(id+"F0.wireOp",EDGE,"E8.28.3"),sQuery(id+"F0.wireOp",EDGE,"E8.29.0"),sQuery(id+"F0.wireOp",EDGE,"E8.29.1"),sQuery(id+"F0.wireOp",EDGE,"E8.29.2"),sQuery(id+"F0.wireOp",EDGE,"E8.29.3"),sQuery(id+"F0.wireOp",EDGE,"E8.30.0"),sQuery(id+"F0.wireOp",EDGE,"E8.30.1"),sQuery(id+"F0.wireOp",EDGE,"E8.30.2"),sQuery(id+"F0.wireOp",EDGE,"E8.30.3"),sQuery(id+"F0.wireOp",EDGE,"E8.31.0"),sQuery(id+"F0.wireOp",EDGE,"E8.31.1"),sQuery(id+"F0.wireOp",EDGE,"E8.31.2"),sQuery(id+"F0.wireOp",EDGE,"E8.31.3"),sQuery(id+"F0.wireOp",EDGE,"E8.32.0"),sQuery(id+"F0.wireOp",EDGE,"E8.32.1"),sQuery(id+"F0.wireOp",EDGE,"E8.32.2"),sQuery(id+"F0.wireOp",EDGE,"E8.32.3"),sQuery(id+"F0.wireOp",EDGE,"E8.33.0"),sQuery(id+"F0.wireOp",EDGE,"E8.33.1"),sQuery(id+"F0.wireOp",EDGE,"E8.33.2"),sQuery(id+"F0.wireOp",EDGE,"E8.33.3"),sQuery(id+"F0.wireOp",EDGE,"E8.34.0"),sQuery(id+"F0.wireOp",EDGE,"E8.34.1"),sQuery(id+"F0.wireOp",EDGE,"E8.34.2"),sQuery(id+"F0.wireOp",EDGE,"E8.34.3"),sQuery(id+"F0.wireOp",EDGE,"E8.35.0"),sQuery(id+"F0.wireOp",EDGE,"E8.35.1"),sQuery(id+"F0.wireOp",EDGE,"E8.35.2"),sQuery(id+"F0.wireOp",EDGE,"E8.35.3"),sQuery(id+"F0.wireOp",EDGE,"E8.36.0"),sQuery(id+"F0.wireOp",EDGE,"E8.36.1"),sQuery(id+"F0.wireOp",EDGE,"E8.36.2"),sQuery(id+"F0.wireOp",EDGE,"E8.36.3"),sQuery(id+"F0.wireOp",EDGE,"E8.37.0"),sQuery(id+"F0.wireOp",EDGE,"E8.37.1"),sQuery(id+"F0.wireOp",EDGE,"E8.37.2"),sQuery(id+"F0.wireOp",EDGE,"E8.37.3"),sQuery(id+"F0.wireOp",EDGE,"E8.38.0"),sQuery(id+"F0.wireOp",EDGE,"E8.38.1"),sQuery(id+"F0.wireOp",EDGE,"E8.38.2"),sQuery(id+"F0.wireOp",EDGE,"E8.38.3"),sQuery(id+"F0.wireOp",EDGE,"E8.39.0"),sQuery(id+"F0.wireOp",EDGE,"E8.39.1"),sQuery(id+"F0.wireOp",EDGE,"E8.39.2"),sQuery(id+"F0.wireOp",EDGE,"E8.39.3"),sQuery(id+"F0.wireOp",EDGE,"E8.40.0"),sQuery(id+"F0.wireOp",EDGE,"E8.40.1"),sQuery(id+"F0.wireOp",EDGE,"E8.40.2"),sQuery(id+"F0.wireOp",EDGE,"E8.40.3"),sQuery(id+"F0.wireOp",EDGE,"E8.41.0"),sQuery(id+"F0.wireOp",EDGE,"E8.41.1"),sQuery(id+"F0.wireOp",EDGE,"E8.41.2"),sQuery(id+"F0.wireOp",EDGE,"E8.41.3"),sQuery(id+"F0.wireOp",EDGE,"E8.42.0"),sQuery(id+"F0.wireOp",EDGE,"E8.42.1"),sQuery(id+"F0.wireOp",EDGE,"E8.42.2"),sQuery(id+"F0.wireOp",EDGE,"E8.42.3"),sQuery(id+"F0.wireOp",EDGE,"E8.43.0"),sQuery(id+"F0.wireOp",EDGE,"E8.43.1"),sQuery(id+"F0.wireOp",EDGE,"E8.43.2"),sQuery(id+"F0.wireOp",EDGE,"E8.43.3"),sQuery(id+"F0.wireOp",EDGE,"E8.44.0"),sQuery(id+"F0.wireOp",EDGE,"E8.44.1"),sQuery(id+"F0.wireOp",EDGE,"E8.44.2"),sQuery(id+"F0.wireOp",EDGE,"E8.44.3"),sQuery(id+"F0.wireOp",EDGE,"E8.45.0"),sQuery(id+"F0.wireOp",EDGE,"E8.45.1"),sQuery(id+"F0.wireOp",EDGE,"E8.45.2"),sQuery(id+"F0.wireOp",EDGE,"E8.45.3"),sQuery(id+"F0.wireOp",EDGE,"E8.46.0"),sQuery(id+"F0.wireOp",EDGE,"E8.46.1"),sQuery(id+"F0.wireOp",EDGE,"E8.46.2"),sQuery(id+"F0.wireOp",EDGE,"E8.46.3"),sQuery(id+"F0.wireOp",EDGE,"E8.47.0"),sQuery(id+"F0.wireOp",EDGE,"E8.47.1"),sQuery(id+"F0.wireOp",EDGE,"E8.47.2"),sQuery(id+"F0.wireOp",EDGE,"E8.47.3"),sQuery(id+"F0.wireOp",EDGE,"E8.48.0"),sQuery(id+"F0.wireOp",EDGE,"E8.48.1"),sQuery(id+"F0.wireOp",EDGE,"E8.48.2"),sQuery(id+"F0.wireOp",EDGE,"E8.48.3"),sQuery(id+"F0.wireOp",EDGE,"E8.49.0"),sQuery(id+"F0.wireOp",EDGE,"E8.49.1"),sQuery(id+"F0.wireOp",EDGE,"E8.49.2"),sQuery(id+"F0.wireOp",EDGE,"E8.49.3")])],"isStart":false});
            var sketch = newSketch(context, id + "F2", { "sketchPlane" : qUnion([Q0])});
            skCircle(sketch, "E9", {"center": v(0, 0) * mm, "radius": 32.5 * mm});
            skSolve(sketch);
        }
        {
            var Q0;
            Q0=qSketchRegion(id+"F2",true);
            extrude(context, id + "F3", {"entities" : qUnion([Q0]), "depth" : 27 * mm, "offsetDistance" : 25.4 * mm});
        }
        {
            var Q0;
            Q0=makeQuery(id+"F3.opExtrude","CAP_FACE",FACE,{"disambiguationData":[OSD([sQuery(id+"F2.wireOp",EDGE,"E9")])],"isStart":false});
            var sketch = newSketch(context, id + "F4", { "sketchPlane" : qUnion([Q0])});
            skCircle(sketch, "E10", {"center": v(0, 0) * mm, "radius": 11.5 * mm});
            skSolve(sketch);
        }
        {
            var Q0;
            Q0=makeQuery(id+"F4.imprint","IMPRINT",FACE,{"disambiguationData":[TD([[makeQuery(id+"F4.imprint","IMPRINT",EDGE,{"derivedFrom":sQuery(id+"F4.wireOp",EDGE,"E10")}),1.0]])]});
            extrude(context, id + "F5", {"entities" : qUnion([Q0]), "depth" : 10 * mm, "offsetDistance" : 25.4 * mm});
        }
        {
            var Q0;
            Q0=qCreatedBy(makeId("Top.planeOp"),FACE);
            var sketch = newSketch(context, id + "F6", { "sketchPlane" : qUnion([Q0])});
            skCircle(sketch, "E11", {"center": v(0, 0) * mm, "radius": 27.5 * mm, "construction": true});
            skLineSegment(sketch, "E12", {"start": v(-5, -27.04) * mm, "end": v(-5, -31.69) * mm});
            skLineSegment(sketch, "E13", {"start": v(-4.5, -32.19) * mm, "end": v(4.5, -32.19) * mm});
            skLineSegment(sketch, "E14", {"start": v(5, -31.69) * mm, "end": v(5, -27.04) * mm});
            skLineSegment(sketch, "E15", {"start": v(0, -32.19) * mm, "end": v(0, 0) * mm, "construction": true});
            skPoint(sketch, "E16.visualSharp", {"position": v(-5, -32.19) * mm});
            skArc(sketch, "E16.filletArc", {"start": v(-5, -31.69) * mm, "mid": v(-4.85, -32.04) * mm, "end": v(-4.5, -32.19) * mm});
            skPoint(sketch, "E17.visualSharp", {"position": v(5, -32.19) * mm});
            skArc(sketch, "E17.filletArc", {"start": v(4.5, -32.19) * mm, "mid": v(4.85, -32.04) * mm, "end": v(5, -31.69) * mm});
            skCircle(sketch, "E18", {"center": v(0, 0) * mm, "radius": 25 * mm});
            skLineSegment(sketch, "E19", {"start": v(0, -32.19) * mm, "end": v(0, -25) * mm, "construction": true});
            skCircle(sketch, "E20", {"center": v(0, -28.6) * mm, "radius": 2.5 * mm});
            skArc(sketch, "E21", {"start": v(5, -27.04) * mm, "mid": v(19.45, -19.45) * mm, "end": v(27.04, -5) * mm});
            skLineSegment(sketch, "E22.1.0", {"start": v(27.04, -5) * mm, "end": v(31.69, -5) * mm});
            skArc(sketch, "E22.1.1", {"start": v(31.69, -5) * mm, "mid": v(32.04, -4.85) * mm, "end": v(32.19, -4.5) * mm});
            skLineSegment(sketch, "E22.1.2", {"start": v(32.19, -4.5) * mm, "end": v(32.19, 4.5) * mm});
            skArc(sketch, "E22.1.3", {"start": v(32.19, 4.5) * mm, "mid": v(32.04, 4.85) * mm, "end": v(31.69, 5) * mm});
            skLineSegment(sketch, "E22.1.4", {"start": v(31.69, 5) * mm, "end": v(27.04, 5) * mm});
            skArc(sketch, "E22.1.5", {"start": v(27.04, 5) * mm, "mid": v(19.45, 19.45) * mm, "end": v(5, 27.04) * mm});
            skLineSegment(sketch, "E22.2.0", {"start": v(5, 27.04) * mm, "end": v(5, 31.69) * mm});
            skArc(sketch, "E22.2.1", {"start": v(5, 31.69) * mm, "mid": v(4.85, 32.04) * mm, "end": v(4.5, 32.19) * mm});
            skLineSegment(sketch, "E22.2.2", {"start": v(4.5, 32.19) * mm, "end": v(-4.5, 32.19) * mm});
            skArc(sketch, "E22.2.3", {"start": v(-4.5, 32.19) * mm, "mid": v(-4.85, 32.04) * mm, "end": v(-5, 31.69) * mm});
            skLineSegment(sketch, "E22.2.4", {"start": v(-5, 31.69) * mm, "end": v(-5, 27.04) * mm});
            skArc(sketch, "E22.2.5", {"start": v(-5, 27.04) * mm, "mid": v(-19.45, 19.45) * mm, "end": v(-27.04, 5) * mm});
            skLineSegment(sketch, "E22.3.0", {"start": v(-27.04, 5) * mm, "end": v(-31.69, 5) * mm});
            skArc(sketch, "E22.3.1", {"start": v(-31.69, 5) * mm, "mid": v(-32.04, 4.85) * mm, "end": v(-32.19, 4.5) * mm});
            skLineSegment(sketch, "E22.3.2", {"start": v(-32.19, 4.5) * mm, "end": v(-32.19, -4.5) * mm});
            skArc(sketch, "E22.3.3", {"start": v(-32.19, -4.5) * mm, "mid": v(-32.04, -4.85) * mm, "end": v(-31.69, -5) * mm});
            skLineSegment(sketch, "E22.3.4", {"start": v(-31.69, -5) * mm, "end": v(-27.04, -5) * mm});
            skArc(sketch, "E22.3.5", {"start": v(-27.04, -5) * mm, "mid": v(-19.45, -19.45) * mm, "end": v(-5, -27.04) * mm});
            skCircle(sketch, "E23.1.0", {"center": v(28.6, 0) * mm, "radius": 2.5 * mm});
            skCircle(sketch, "E23.2.0", {"center": v(0, 28.6) * mm, "radius": 2.5 * mm});
            skCircle(sketch, "E23.3.0", {"center": v(-28.6, 0) * mm, "radius": 2.5 * mm});
            skSolve(sketch);
        }
        {
            var Q0;
            Q0=qSketchRegion(id+"F6",true);
            extrude(context, id + "F7", {"entities" : qUnion([Q0]), "oppositeDirection" : true, "depth" : 8 * mm, "offsetDistance" : 25.4 * mm});
        }
        {
            var Q0;
            Q0=makeQuery(id+"F7.opExtrude","CAP_FACE",FACE,{"disambiguationData":[OSD([sQuery(id+"F6.wireOp",EDGE,"E12"),sQuery(id+"F6.wireOp",EDGE,"E13"),sQuery(id+"F6.wireOp",EDGE,"E14"),sQuery(id+"F6.wireOp",EDGE,"E16.filletArc"),sQuery(id+"F6.wireOp",EDGE,"E17.filletArc"),sQuery(id+"F6.wireOp",EDGE,"E18"),sQuery(id+"F6.wireOp",EDGE,"E20"),sQuery(id+"F6.wireOp",EDGE,"E21"),sQuery(id+"F6.wireOp",EDGE,"E22.1.0"),sQuery(id+"F6.wireOp",EDGE,"E22.1.1"),sQuery(id+"F6.wireOp",EDGE,"E22.1.2"),sQuery(id+"F6.wireOp",EDGE,"E22.1.3"),sQuery(id+"F6.wireOp",EDGE,"E22.1.4"),sQuery(id+"F6.wireOp",EDGE,"E22.1.5"),sQuery(id+"F6.wireOp",EDGE,"E22.2.0"),sQuery(id+"F6.wireOp",EDGE,"E22.2.1"),sQuery(id+"F6.wireOp",EDGE,"E22.2.2"),sQuery(id+"F6.wireOp",EDGE,"E22.2.3"),sQuery(id+"F6.wireOp",EDGE,"E22.2.4"),sQuery(id+"F6.wireOp",EDGE,"E22.2.5"),sQuery(id+"F6.wireOp",EDGE,"E22.3.0"),sQuery(id+"F6.wireOp",EDGE,"E22.3.1"),sQuery(id+"F6.wireOp",EDGE,"E22.3.2"),sQuery(id+"F6.wireOp",EDGE,"E22.3.3"),sQuery(id+"F6.wireOp",EDGE,"E22.3.4"),sQuery(id+"F6.wireOp",EDGE,"E22.3.5"),sQuery(id+"F6.wireOp",EDGE,"E23.1.0"),sQuery(id+"F6.wireOp",EDGE,"E23.2.0"),sQuery(id+"F6.wireOp",EDGE,"E23.3.0")])],"isStart":false});
            var sketch = newSketch(context, id + "F8", { "sketchPlane" : qUnion([Q0])});
            skCircle(sketch, "E24", {"center": v(0, 0) * mm, "radius": 25 * mm});
            skSolve(sketch);
        }
        {
            var Q0;
            Q0=qSketchRegion(id+"F8",true);
            extrude(context, id + "F9", {"entities" : qUnion([Q0]), "depth" : 11 * mm, "offsetDistance" : 25.4 * mm});
        }
        {
            var Q0;
            Q0=makeQuery(id+"F9.opExtrude","CAP_FACE",FACE,{"disambiguationData":[OSD([sQuery(id+"F8.wireOp",EDGE,"E24")])],"isStart":false});
            var sketch = newSketch(context, id + "F10", { "sketchPlane" : qUnion([Q0])});
            skCircle(sketch, "E25", {"center": v(0, 0) * mm, "radius": 25 * mm});
            skSolve(sketch);
        }
        {
            var Q0;
            Q0=qSketchRegion(id+"F10",true);
            extrude(context, id + "F11", {"entities" : qUnion([Q0]), "depth" : 7 * mm, "offsetDistance" : 25.4 * mm});
        }
        {
            var Q0;
            Q0=makeQuery(id+"F11.opExtrude","CAP_FACE",FACE,{"disambiguationData":[OSD([sQuery(id+"F10.wireOp",EDGE,"E25")])],"isStart":false});
            var sketch = newSketch(context, id + "F12", { "sketchPlane" : qUnion([Q0])});
            skCircle(sketch, "E26", {"center": v(0, 0) * mm, "radius": 15 * mm});
            skSolve(sketch);
        }
        {
            var Q0;
            Q0=qSketchRegion(id+"F12",true);
            extrude(context, id + "F13", {"entities" : qUnion([Q0]), "depth" : 4 * mm, "offsetDistance" : 25.4 * mm});
        }
        {
            var Q0;
            Q0=makeQuery(id+"F13.opExtrude","CAP_FACE",FACE,{"disambiguationData":[OSD([sQuery(id+"F12.wireOp",EDGE,"E26")])],"isStart":false});
            var sketch = newSketch(context, id + "F14", { "sketchPlane" : qUnion([Q0])});
            skCircle(sketch, "E27", {"center": v(0, 0) * mm, "radius": 7.5 * mm});
            skSolve(sketch);
        }
        {
            var Q0;
            Q0=makeQuery(id+"F14.imprint","IMPRINT",FACE,{"disambiguationData":[TD([[makeQuery(id+"F14.imprint","IMPRINT",EDGE,{"derivedFrom":sQuery(id+"F14.wireOp",EDGE,"E27")}),1.0]])]});
            var Q1;
            Q1=sQuery(id+"F14.wireOp",EDGE,"E27");
            extrude(context, id + "F15", {"entities" : qUnion([Q0]), "surfaceEntities" : qUnion([Q1]), "depth" : 13 * mm, "offsetDistance" : 25.4 * mm});
        }
        {
            var Q0;
            Q0=makeQuery(id+"F15.opExtrude","CAP_FACE",FACE,{"disambiguationData":[OSD([sQuery(id+"F14.wireOp",EDGE,"E27")])],"isStart":false});
            var sketch = newSketch(context, id + "F16", { "sketchPlane" : qUnion([Q0])});
            skCircle(sketch, "E28", {"center": v(0, 0) * mm, "radius": 12.5 * mm});
            skCircle(sketch, "E29", {"center": v(0, 0) * mm, "radius": 5.5 * mm});
            skSolve(sketch);
        }
        {
            var Q0;
            Q0=qSketchRegion(id+"F16",true);
            extrude(context, id + "F17", {"entities" : qUnion([Q0]), "depth" : 12 * mm, "offsetDistance" : 25.4 * mm});
        }
    });
